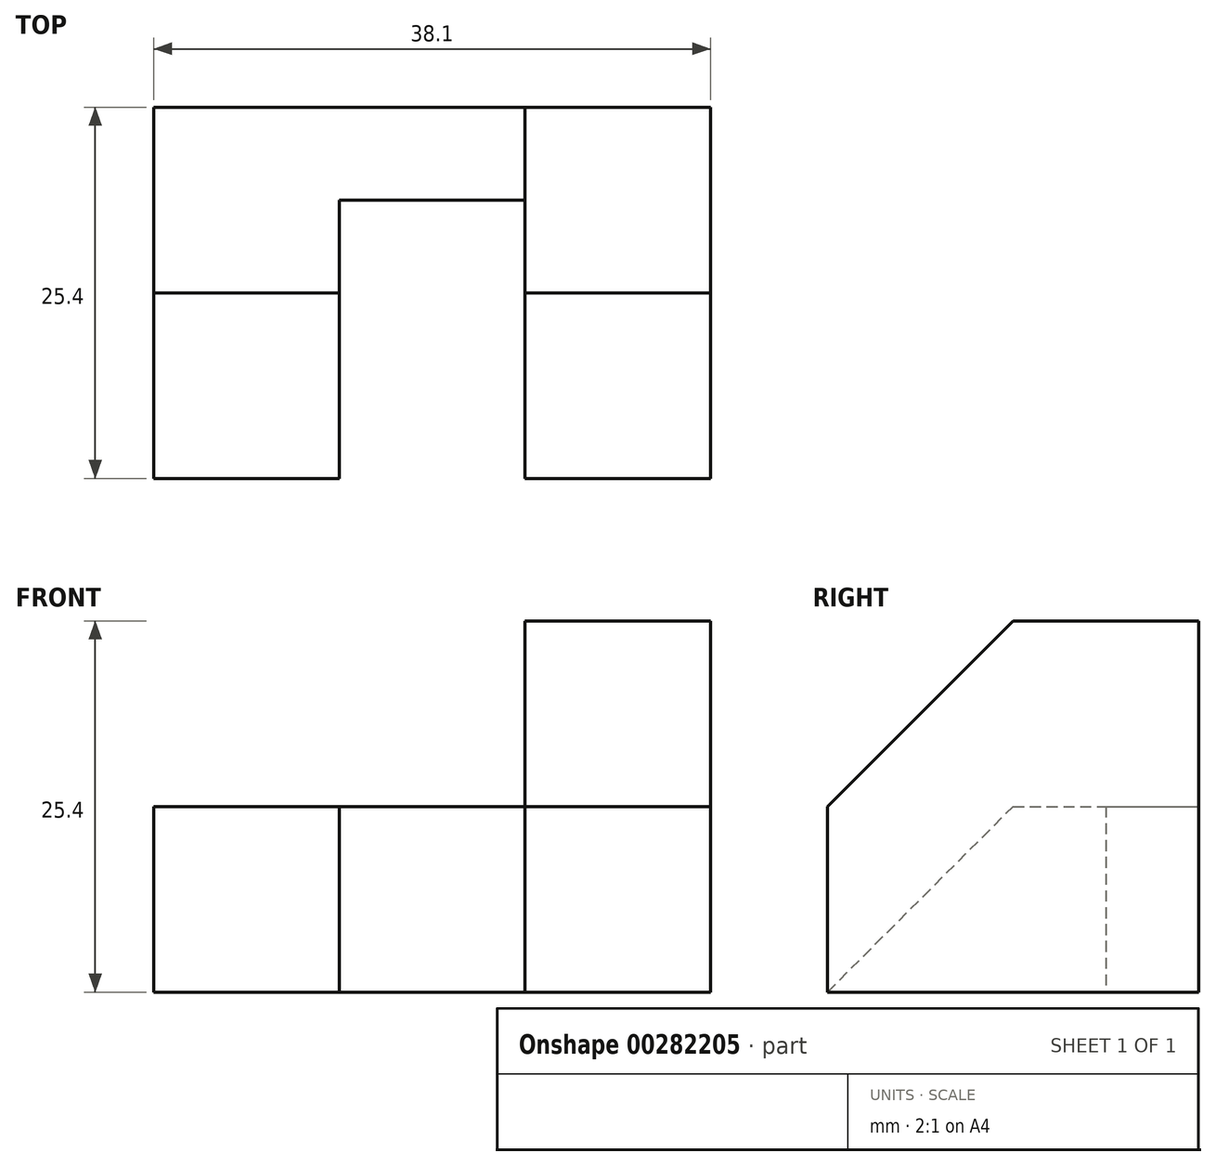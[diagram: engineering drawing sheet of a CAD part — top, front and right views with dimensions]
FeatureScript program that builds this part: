
annotation { "Feature Type Name" : "Feature", "Feature Type Description" : "" }
export const myFeature = defineFeature(function(context is Context, id is Id, definition is map)
    precondition{}
    {
        {
            var Q0;
            Q0=qCreatedBy(makeId("Right.planeOp"),FACE);
            var sketch = newSketch(context, id + "F0", { "sketchPlane" : qUnion([Q0])});
            skLineSegment(sketch, "E0", {"start": v(0, 0) * mm, "end": v(12.7, 12.7) * mm});
            skLineSegment(sketch, "E1", {"start": v(12.7, 12.7) * mm, "end": v(12.7, 0) * mm});
            skLineSegment(sketch, "E2", {"start": v(0, 0) * mm, "end": v(12.7, 0) * mm});
            skSolve(sketch);
        }
        {
            var Q0;
            Q0 = qSketchRegion(id + "F0", true);
            extrude(context, id + "F1", {"entities" : qUnion([Q0]), "depth" : 12.7 * mm});
        }
        {
            var Q0;
            Q0=qCreatedBy(makeId("Right.planeOp"),FACE);
            var sketch = newSketch(context, id + "F2", { "sketchPlane" : qUnion([Q0])});
            skLineSegment(sketch, "E3.bottom", {"start": v(12.7, 12.7) * mm, "end": v(25.4, 12.7) * mm});
            skLineSegment(sketch, "E3.top", {"start": v(12.7, 0) * mm, "end": v(25.4, 0) * mm});
            skLineSegment(sketch, "E3.left", {"start": v(12.7, 12.7) * mm, "end": v(12.7, 0) * mm});
            skLineSegment(sketch, "E3.right", {"start": v(25.4, 12.7) * mm, "end": v(25.4, 0) * mm});
            skSolve(sketch);
        }
        {
            var Q0;
            Q0 = qSketchRegion(id + "F2", true);
            extrude(context, id + "F3", {"entities" : qUnion([Q0]), "operationType" : NewBodyOperationType.ADD, "depth" : 12.7 * mm});
        }
        {
            var Q0;
            Q0=makeQuery(id+"F3.boolean.opBoolean","MERGE",FACE,{"derivedFrom":[makeQuery(id+"F1.opExtrude","CAP_FACE",FACE,{"disambiguationData":[OSD([sQuery(id+"F0.wireOp",EDGE,"E0"),sQuery(id+"F0.wireOp",EDGE,"E1"),sQuery(id+"F0.wireOp",EDGE,"E2")])],"isStart":false}),makeQuery(id+"F3.opExtrude","CAP_FACE",FACE,{"disambiguationData":[OSD([sQuery(id+"F2.wireOp",EDGE,"E3.bottom"),sQuery(id+"F2.wireOp",EDGE,"E3.top"),sQuery(id+"F2.wireOp",EDGE,"E3.left"),sQuery(id+"F2.wireOp",EDGE,"E3.right")])],"isStart":false})]});
            var sketch = newSketch(context, id + "F4", { "sketchPlane" : qUnion([Q0])});
            skLineSegment(sketch, "E4.bottom", {"start": v(19.05, 12.7) * mm, "end": v(25.4, 12.7) * mm});
            skLineSegment(sketch, "E4.top", {"start": v(19.05, 0) * mm, "end": v(25.4, 0) * mm});
            skLineSegment(sketch, "E4.left", {"start": v(19.05, 12.7) * mm, "end": v(19.05, 0) * mm});
            skLineSegment(sketch, "E4.right", {"start": v(25.4, 12.7) * mm, "end": v(25.4, 0) * mm});
            skSolve(sketch);
        }
        {
            var Q0;
            Q0 = qSketchRegion(id + "F4", true);
            extrude(context, id + "F5", {"entities" : qUnion([Q0]), "operationType" : NewBodyOperationType.ADD, "depth" : 12.7 * mm});
        }
        {
            var Q0;
            Q0=makeQuery(id+"F5.opExtrude","CAP_FACE",FACE,{"disambiguationData":[OSD([sQuery(id+"F4.wireOp",EDGE,"E4.bottom"),sQuery(id+"F4.wireOp",EDGE,"E4.top"),sQuery(id+"F4.wireOp",EDGE,"E4.left"),sQuery(id+"F4.wireOp",EDGE,"E4.right")])],"isStart":false});
            var sketch = newSketch(context, id + "F6", { "sketchPlane" : qUnion([Q0])});
            skLineSegment(sketch, "E5.bottom", {"start": v(25.4, 0) * mm, "end": v(0, 0) * mm});
            skLineSegment(sketch, "E5.top", {"start": v(25.4, 25.4) * mm, "end": v(0, 25.4) * mm});
            skLineSegment(sketch, "E5.left", {"start": v(25.4, 0) * mm, "end": v(25.4, 25.4) * mm});
            skLineSegment(sketch, "E5.right", {"start": v(0, 0) * mm, "end": v(0, 25.4) * mm});
            skSolve(sketch);
        }
        {
            var Q0;
            Q0 = qSketchRegion(id + "F6", true);
            extrude(context, id + "F7", {"entities" : qUnion([Q0]), "operationType" : NewBodyOperationType.ADD, "depth" : 12.7 * mm});
        }
        {
            var Q0;
            Q0=makeQuery(id+"F7.opExtrude","CAP_FACE",FACE,{"disambiguationData":[OSD([sQuery(id+"F6.wireOp",EDGE,"E5.bottom"),sQuery(id+"F6.wireOp",EDGE,"E5.top"),sQuery(id+"F6.wireOp",EDGE,"E5.left"),sQuery(id+"F6.wireOp",EDGE,"E5.right")])],"isStart":false});
            var sketch = newSketch(context, id + "F8", { "sketchPlane" : qUnion([Q0])});
            skLineSegment(sketch, "E6", {"start": v(0, 12.7) * mm, "end": v(12.7, 25.4) * mm});
            skLineSegment(sketch, "E7", {"start": v(0, 12.7) * mm, "end": v(0, 25.4) * mm});
            skLineSegment(sketch, "E8", {"start": v(0, 25.4) * mm, "end": v(12.7, 25.4) * mm});
            skSolve(sketch);
        }
        {
            var Q0;
            Q0 = qSketchRegion(id + "F8", true);
            extrude(context, id + "F9", {"entities" : qUnion([Q0]), "operationType" : NewBodyOperationType.REMOVE, "oppositeDirection" : true, "depth" : 12.7 * mm});
        }
    });
